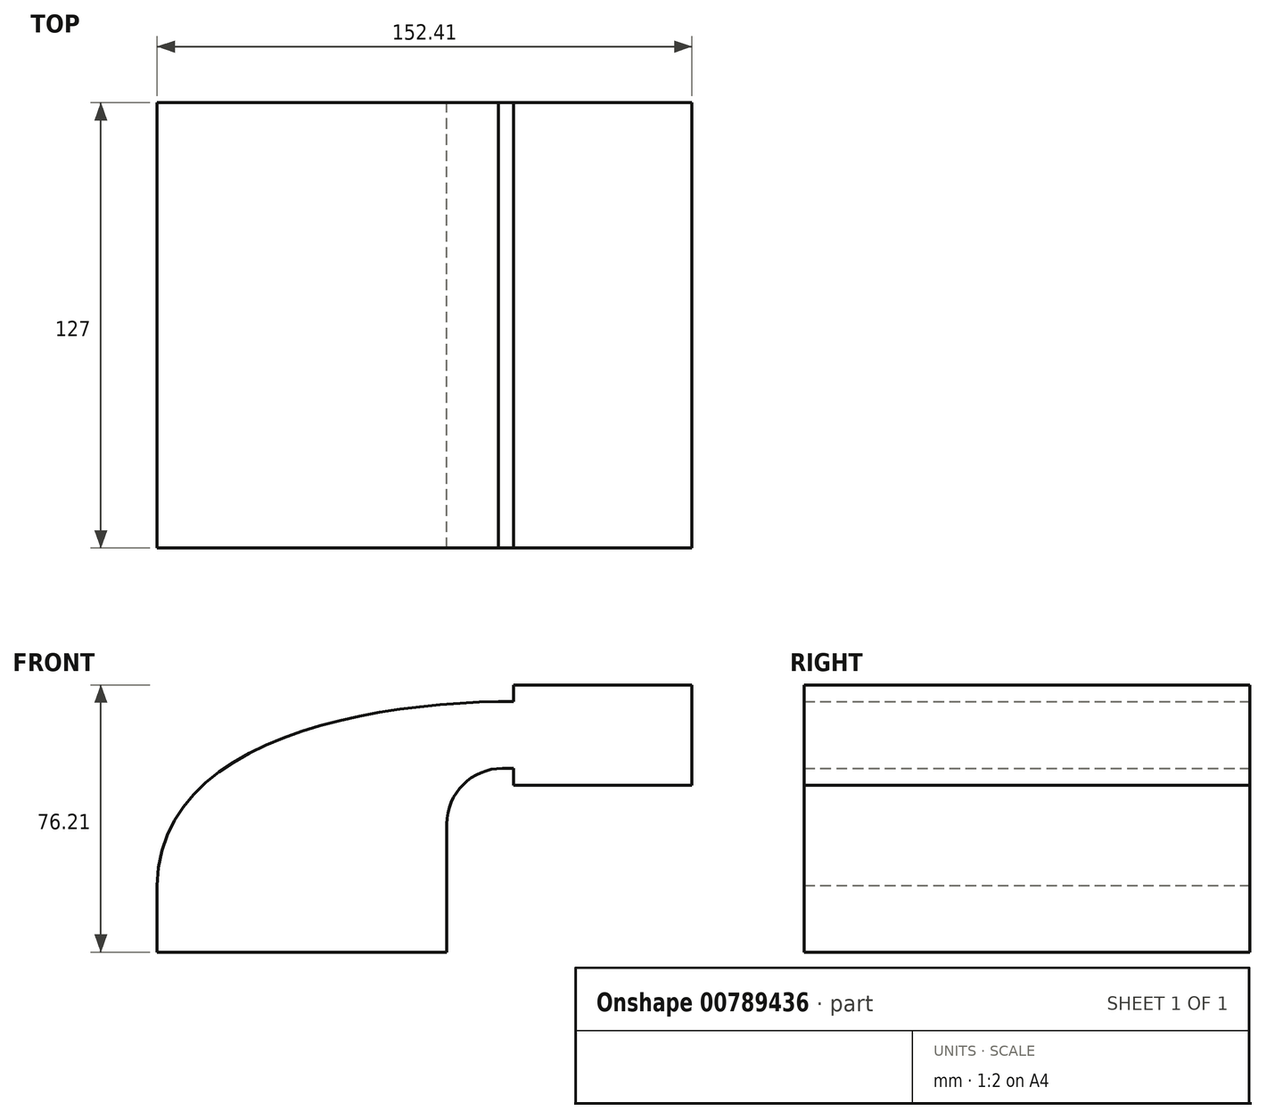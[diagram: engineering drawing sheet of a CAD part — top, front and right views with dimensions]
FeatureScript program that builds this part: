
annotation { "Feature Type Name" : "Feature", "Feature Type Description" : "" }
export const myFeature = defineFeature(function(context is Context, id is Id, definition is map)
    precondition{}
    {
        {
            var Q0;
            Q0=qCreatedBy(makeId("Front.planeOp"),FACE);
            var sketch = newSketch(context, id + "F0", { "sketchPlane" : qUnion([Q0])});
            skLineSegment(sketch, "E0.bottom", {"start": v(-41.28, -9.53) * mm, "end": v(41.28, -9.53) * mm});
            skLineSegment(sketch, "E0.top", {"start": v(-41.28, 9.53) * mm, "end": v(41.28, 9.53) * mm});
            skLineSegment(sketch, "E0.left", {"start": v(-41.28, -9.53) * mm, "end": v(-41.28, 9.53) * mm});
            skLineSegment(sketch, "E0.right", {"start": v(41.28, -9.53) * mm, "end": v(41.28, 9.53) * mm});
            skPoint(sketch, "E0.middle", {"position": v(0, 0) * mm});
            skLineSegment(sketch, "E1.bottom", {"start": v(60.32, 38.1) * mm, "end": v(111.12, 38.1) * mm});
            skLineSegment(sketch, "E1.top", {"start": v(60.32, 66.67) * mm, "end": v(111.12, 66.67) * mm});
            skLineSegment(sketch, "E1.left", {"start": v(60.32, 38.1) * mm, "end": v(60.32, 66.67) * mm});
            skLineSegment(sketch, "E1.right", {"start": v(111.12, 38.1) * mm, "end": v(111.12, 66.67) * mm});
            skPoint(sketch, "E1.middle", {"position": v(85.72, 52.39) * mm});
            skLineSegment(sketch, "E2", {"start": v(41.27, 9.53) * mm, "end": v(41.27, 27) * mm});
            skArc(sketch, "E3", {"start": v(41.27, 27) * mm, "mid": v(45.92, 38.23) * mm, "end": v(57.15, 42.88) * mm});
            skLineSegment(sketch, "E4", {"start": v(57.15, 42.88) * mm, "end": v(85.47, 42.88) * mm});
            skLineSegment(sketch, "E5", {"start": v(85.72, 38.1) * mm, "end": v(85.72, 66.67) * mm});
            skLineSegment(sketch, "E6.0", {"start": v(57.15, 61.93) * mm, "end": v(85.47, 61.93) * mm});
            skArc(sketch, "E6.1", {"start": v(22.23, 27) * mm, "mid": v(32.45, 51.7) * mm, "end": v(57.15, 61.93) * mm});
            skLineSegment(sketch, "E6.2", {"start": v(22.22, 9.53) * mm, "end": v(22.22, 27) * mm});
            skFitSpline(sketch, "E7", {"points": [v(-41.28, 9.53) * mm, v(57.15, 61.93) * mm], "startDerivative": vector(1.47, 121.73) * mm, "endDerivative": vector(123.66, 1.72) * mm});
            skSolve(sketch);
        }
        {
            var Q0;
            Q0 = qSketchRegion(id + "F0", true);
            extrude(context, id + "F1", {"entities" : qUnion([Q0]), "endBound" : BoundingType.SYMMETRIC, "depth" : 127 * mm, "offsetDistance" : 25.4 * mm});
        }
    });
